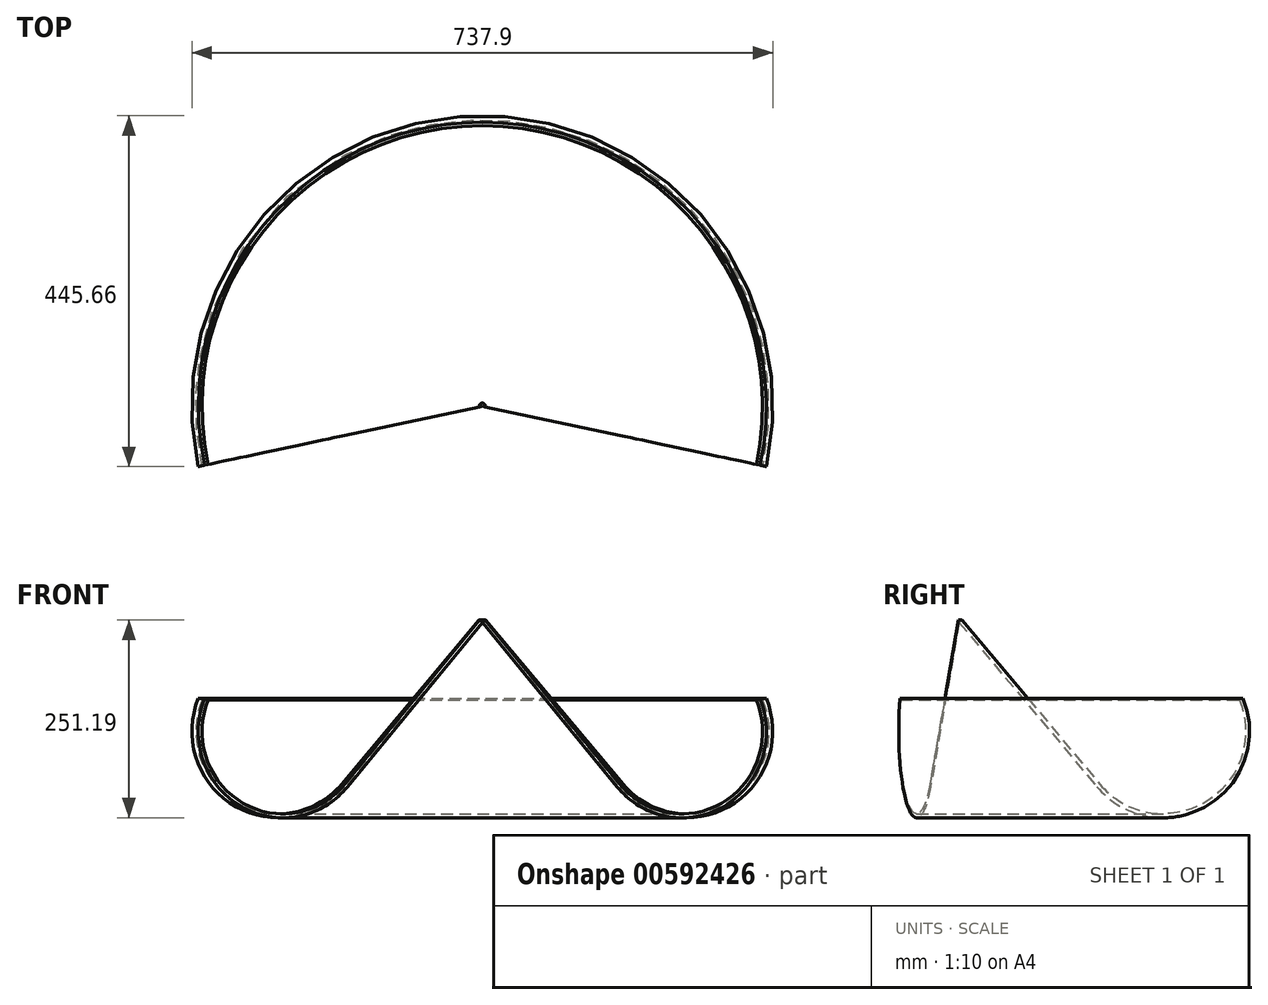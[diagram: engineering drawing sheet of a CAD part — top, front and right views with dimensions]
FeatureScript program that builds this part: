
annotation { "Feature Type Name" : "Feature", "Feature Type Description" : "" }
export const myFeature = defineFeature(function(context is Context, id is Id, definition is map)
    precondition{}
    {
        {
            var Q0;
            Q0=qCreatedBy(makeId("Top.planeOp"),FACE);
            var sketch = newSketch(context, id + "F0", { "sketchPlane" : qUnion([Q0])});
            skLineSegment(sketch, "E0", {"start": v(0, 0) * mm, "end": v(-1956.3, -415.82) * mm, "construction": true});
            skLineSegment(sketch, "E1", {"start": v(0, 0) * mm, "end": v(0, 15282.18) * mm, "construction": true});
            skLineSegment(sketch, "E2", {"start": v(0, 0) * mm, "end": v(-1948.74, 449.9) * mm, "construction": true});
            skLineSegment(sketch, "E3", {"start": v(-1948.74, 449.9) * mm, "end": v(-243.6, 56.24) * mm});
            skLineSegment(sketch, "E4", {"start": v(-1956.3, -415.82) * mm, "end": v(-244.54, -51.98) * mm});
            skSolve(sketch);
        }
        {
            var Q0;
            Q0=qCreatedBy(makeId("Right.planeOp"),FACE);
            var sketch = newSketch(context, id + "F1", { "sketchPlane" : qUnion([Q0])});
            skLineSegment(sketch, "E5", {"start": v(0, 0) * mm, "end": v(360.75, -96.66) * mm, "construction": true});
            skLineSegment(sketch, "E6", {"start": v(0, 0) * mm, "end": v(175.2, -208.8) * mm});
            skArc(sketch, "E7", {"start": v(175.2, -208.8) * mm, "mid": v(315.98, -232.17) * mm, "end": v(360.75, -96.66) * mm});
            skLineSegment(sketch, "E8", {"start": v(0, 0) * mm, "end": v(0, 159.77) * mm, "construction": true});
            skArc(sketch, "E9.0", {"start": v(179.03, -205.58) * mm, "mid": v(313.4, -227.9) * mm, "end": v(356.12, -98.56) * mm});
            skLineSegment(sketch, "E9.1", {"start": v(3.83, 3.21) * mm, "end": v(179.03, -205.58) * mm});
            skLineSegment(sketch, "E10", {"start": v(360.75, -96.66) * mm, "end": v(356.12, -98.56) * mm});
            skLineSegment(sketch, "E11", {"start": v(3.83, 3.21) * mm, "end": v(0, 0) * mm});
            skSolve(sketch);
        }
        {
            var Q0;
            Q0=makeQuery(id+"F1.imprint","IMPRINT",FACE,{"disambiguationData":[TD([[makeQuery(id+"F1.imprint","IMPRINT",EDGE,{"derivedFrom":sQuery(id+"F1.wireOp",EDGE,"E5")}),-1.0]])]});
            var Q1;
            Q1=makeQuery(id+"F1.imprint","IMPRINT",FACE,{"disambiguationData":[TD([[makeQuery(id+"F1.imprint","IMPRINT",EDGE,{"derivedFrom":sQuery(id+"F1.wireOp",EDGE,"E6")}),1.0]])]});
            var Q2;
            Q2=sQuery(id+"F1.wireOp",EDGE,"E8");
            revolve(context, id + "F2", {"entities" : qUnion([Q0, Q1]), "axis" : qUnion([Q2]), "revolveType" : RevolveType.SYMMETRIC, "angle" : 204 * degree});
        }
    });
